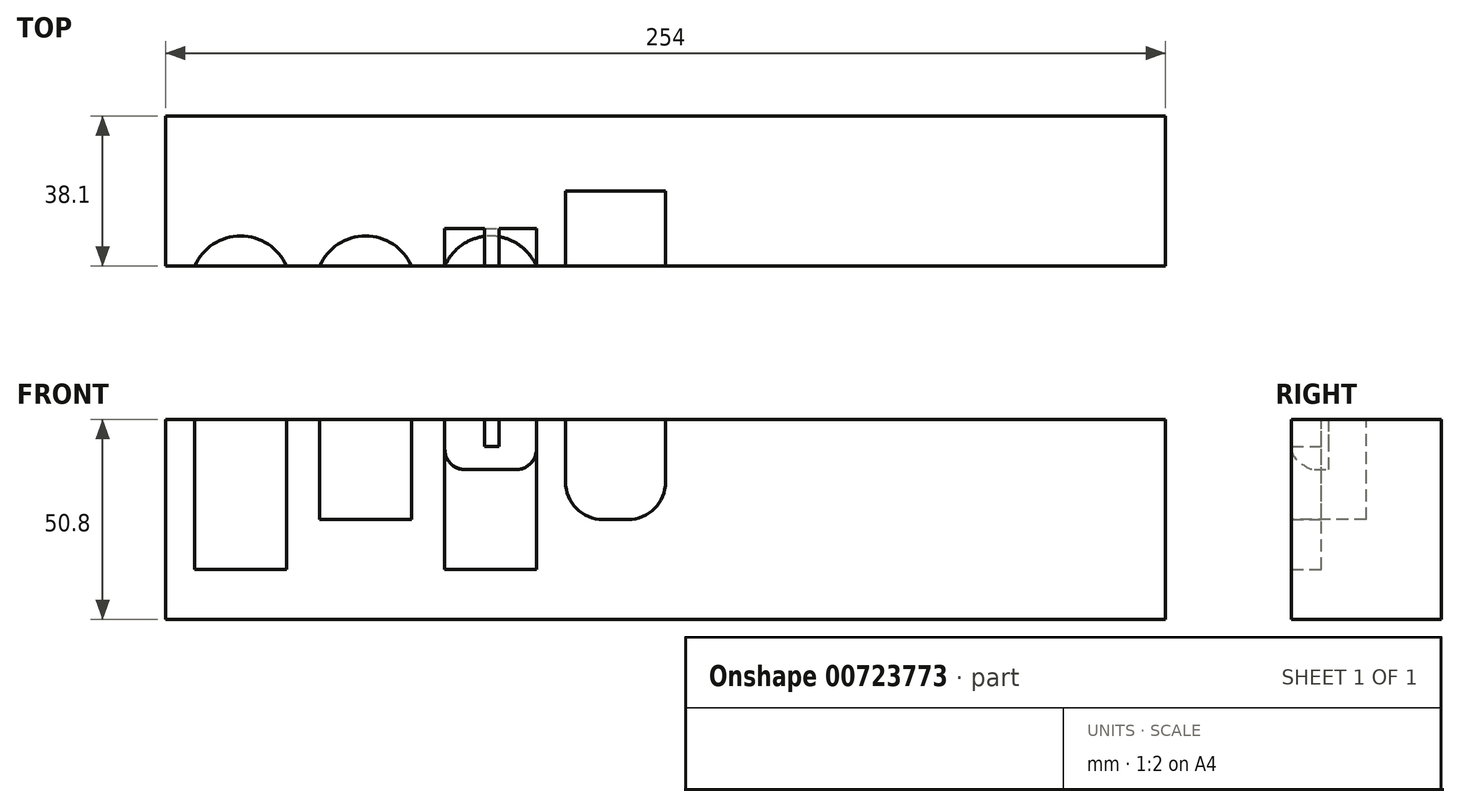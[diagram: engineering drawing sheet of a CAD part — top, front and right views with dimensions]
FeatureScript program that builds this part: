
annotation { "Feature Type Name" : "Feature", "Feature Type Description" : "" }
export const myFeature = defineFeature(function(context is Context, id is Id, definition is map)
    precondition{}
    {
        {
            var Q0;
            Q0=qCreatedBy(makeId("Right.planeOp"),FACE);
            var sketch = newSketch(context, id + "F0", { "sketchPlane" : qUnion([Q0])});
            skLineSegment(sketch, "E0.bottom", {"start": v(0, 0) * mm, "end": v(38.1, 0) * mm});
            skLineSegment(sketch, "E0.top", {"start": v(0, 50.8) * mm, "end": v(38.1, 50.8) * mm});
            skLineSegment(sketch, "E0.left", {"start": v(0, 0) * mm, "end": v(0, 50.8) * mm});
            skLineSegment(sketch, "E0.right", {"start": v(38.1, 0) * mm, "end": v(38.1, 50.8) * mm});
            skSolve(sketch);
        }
        {
            var Q0;
            Q0=makeQuery(id+"F0.imprint","IMPRINT",FACE,{"disambiguationData":[TD([[makeQuery(id+"F0.imprint","IMPRINT",EDGE,{"derivedFrom":sQuery(id+"F0.wireOp",EDGE,"E0.bottom")}),1.0]])]});
            extrude(context, id + "F1", {"entities" : qUnion([Q0]), "depth" : 254 * mm, "offsetDistance" : 25.4 * mm});
        }
        {
            var Q0;
            Q0=makeQuery(id+"F1.opExtrude","SWEPT_FACE",FACE,{"disambiguationData":[OSD([sQuery(id+"F0.wireOp",EDGE,"E0.top")])]});
            var sketch = newSketch(context, id + "F2", { "sketchPlane" : qUnion([Q0])});
            skLineSegment(sketch, "E1", {"start": v(0, 0) * mm, "end": v(0, -5.08) * mm});
            skLineSegment(sketch, "E2", {"start": v(0, -5.08) * mm, "end": v(19.05, -5.08) * mm});
            skCircle(sketch, "E3", {"center": v(19.05, -5.08) * mm, "radius": 12.7 * mm});
            skSolve(sketch);
        }
        {
            var Q0;
            Q0 = qSketchRegion(id + "F2", true);
            extrude(context, id + "F3", {"entities" : qUnion([Q0]), "operationType" : NewBodyOperationType.REMOVE, "oppositeDirection" : true, "depth" : 38.1 * mm, "offsetDistance" : 25.4 * mm});
        }
        {
            var Q0;
            Q0=makeQuery(id+"F1.opExtrude","SWEPT_FACE",FACE,{"disambiguationData":[OSD([sQuery(id+"F0.wireOp",EDGE,"E0.top")])]});
            var sketch = newSketch(context, id + "F4", { "sketchPlane" : qUnion([Q0])});
            skLineSegment(sketch, "E4", {"start": v(0, 0) * mm, "end": v(0, -5.08) * mm});
            skLineSegment(sketch, "E5", {"start": v(0, -5.08) * mm, "end": v(50.8, -5.08) * mm});
            skCircle(sketch, "E6", {"center": v(50.8, -5.08) * mm, "radius": 12.7 * mm});
            skSolve(sketch);
        }
        {
            var Q0;
            Q0 = qSketchRegion(id + "F4", true);
            extrude(context, id + "F5", {"entities" : qUnion([Q0]), "operationType" : NewBodyOperationType.REMOVE, "oppositeDirection" : true, "depth" : 25.4 * mm, "offsetDistance" : 25.4 * mm});
        }
        {
            var Q0;
            Q0=makeQuery(id+"F1.opExtrude","SWEPT_FACE",FACE,{"disambiguationData":[OSD([sQuery(id+"F0.wireOp",EDGE,"E0.top")])]});
            var sketch = newSketch(context, id + "F6", { "sketchPlane" : qUnion([Q0])});
            skLineSegment(sketch, "E7", {"start": v(0, 0) * mm, "end": v(0, -5.08) * mm});
            skLineSegment(sketch, "E8", {"start": v(0, -5.08) * mm, "end": v(82.55, -5.08) * mm});
            skCircle(sketch, "E9", {"center": v(82.55, -5.08) * mm, "radius": 12.7 * mm});
            skSolve(sketch);
        }
        {
            var Q0;
            Q0 = qSketchRegion(id + "F6", true);
            extrude(context, id + "F7", {"entities" : qUnion([Q0]), "operationType" : NewBodyOperationType.REMOVE, "oppositeDirection" : true, "depth" : 38.1 * mm, "offsetDistance" : 25.4 * mm});
        }
        {
            var Q0;
            Q0=makeQuery(id+"F1.opExtrude","SWEPT_FACE",FACE,{"disambiguationData":[OSD([sQuery(id+"F0.wireOp",EDGE,"E0.top")])]});
            var sketch = newSketch(context, id + "F8", { "sketchPlane" : qUnion([Q0])});
            skLineSegment(sketch, "E10", {"start": v(0, 0) * mm, "end": v(0, -9.07) * mm});
            skLineSegment(sketch, "E11", {"start": v(70.91, 0) * mm, "end": v(70.91, -18.35) * mm});
            skLineSegment(sketch, "E12", {"start": v(0, -9.07) * mm, "end": v(70.91, -9.07) * mm});
            skPoint(sketch, "E12.endSnap0", {"position": v(70.91, -9.18) * mm});
            skLineSegment(sketch, "E13.bottom", {"start": v(70.91, -9.07) * mm, "end": v(94.19, -9.07) * mm});
            skLineSegment(sketch, "E13.top", {"start": v(70.91, 0) * mm, "end": v(94.19, 0) * mm});
            skLineSegment(sketch, "E13.left", {"start": v(70.91, -9.07) * mm, "end": v(70.91, 0) * mm});
            skLineSegment(sketch, "E13.right", {"start": v(94.19, -9.07) * mm, "end": v(94.19, 0) * mm});
            skLineSegment(sketch, "E14.bottom", {"start": v(94.19, 0) * mm, "end": v(70.91, 0) * mm});
            skLineSegment(sketch, "E14.top", {"start": v(94.19, 9.57) * mm, "end": v(70.91, 9.57) * mm});
            skLineSegment(sketch, "E14.left", {"start": v(94.19, 0) * mm, "end": v(94.19, 9.57) * mm});
            skLineSegment(sketch, "E14.right", {"start": v(70.91, 0) * mm, "end": v(70.91, 9.57) * mm});
            skSolve(sketch);
        }
        {
            var Q0;
            Q0 = qSketchRegion(id + "F8", true);
            extrude(context, id + "F9", {"entities" : qUnion([Q0]), "operationType" : NewBodyOperationType.REMOVE, "oppositeDirection" : true, "depth" : 12.7 * mm, "offsetDistance" : 25.4 * mm});
        }
        {
            var Q0;
            Q0=makeQuery(id+"F9.boolean.opBoolean","COPY",EDGE,{"derivedFrom":makeQuery(id+"F9.opExtrude","CAP_EDGE",EDGE,{"disambiguationData":[OSD([sQuery(id+"F8.wireOp",EDGE,"E13.left"),sQuery(id+"F8.wireOp",EDGE,"E14.right")])],"isStart":false})});
            var Q1;
            Q1=makeQuery(id+"F9.boolean.opBoolean","COPY",EDGE,{"derivedFrom":makeQuery(id+"F9.opExtrude","CAP_EDGE",EDGE,{"disambiguationData":[OSD([sQuery(id+"F8.wireOp",EDGE,"E13.right"),sQuery(id+"F8.wireOp",EDGE,"E14.left")])],"isStart":false})});
            fillet(context, id + "F10", {"entities" : qUnion([Q0, Q1]), "radius" : 5.08 * mm, "tangentPropagation" : true, "allowEdgeOverflow" : false});
        }
        {
            var Q0;
            Q0=makeQuery(id+"F9.boolean.opBoolean","COPY",FACE,{"derivedFrom":makeQuery(id+"F9.opExtrude","SWEPT_FACE",FACE,{"disambiguationData":[OSD([sQuery(id+"F8.wireOp",EDGE,"E14.top")])]})});
            var sketch = newSketch(context, id + "F11", { "sketchPlane" : qUnion([Q0])});
            skLineSegment(sketch, "E15", {"start": v(70.91, 50.8) * mm, "end": v(81.06, 50.8) * mm});
            skLineSegment(sketch, "E16", {"start": v(81.06, 50.8) * mm, "end": v(81.06, 43.95) * mm});
            skLineSegment(sketch, "E17", {"start": v(81.06, 43.95) * mm, "end": v(84.68, 43.95) * mm});
            skLineSegment(sketch, "E18", {"start": v(84.68, 43.95) * mm, "end": v(84.68, 50.8) * mm});
            skLineSegment(sketch, "E19", {"start": v(84.68, 50.8) * mm, "end": v(81.06, 50.8) * mm});
            skSolve(sketch);
        }
        {
            var Q0;
            Q0 = qSketchRegion(id + "F11", true);
            extrude(context, id + "F12", {"entities" : qUnion([Q0]), "operationType" : NewBodyOperationType.ADD, "depth" : 9.52 * mm, "offsetDistance" : 25.4 * mm});
        }
        {
            var Q0;
            Q0=makeQuery(id+"F1.opExtrude","SWEPT_FACE",FACE,{"disambiguationData":[OSD([sQuery(id+"F0.wireOp",EDGE,"E0.left")])]});
            var sketch = newSketch(context, id + "F13", { "sketchPlane" : qUnion([Q0])});
            skLineSegment(sketch, "E20", {"start": v(0, 50.8) * mm, "end": v(0, 38.1) * mm});
            skLineSegment(sketch, "E21", {"start": v(0, 38.1) * mm, "end": v(101.6, 38.1) * mm});
            skLineSegment(sketch, "E22", {"start": v(101.6, 38.1) * mm, "end": v(101.6, 50.8) * mm});
            skLineSegment(sketch, "E23", {"start": v(101.6, 50.8) * mm, "end": v(127, 50.8) * mm});
            skLineSegment(sketch, "E24", {"start": v(127, 50.8) * mm, "end": v(127, 25.4) * mm});
            skLineSegment(sketch, "E25", {"start": v(127, 25.4) * mm, "end": v(101.6, 25.4) * mm});
            skLineSegment(sketch, "E26", {"start": v(101.6, 25.4) * mm, "end": v(101.6, 38.1) * mm});
            skSolve(sketch);
        }
        {
            var Q0;
            Q0 = qSketchRegion(id + "F13", true);
            extrude(context, id + "F14", {"entities" : qUnion([Q0]), "operationType" : NewBodyOperationType.REMOVE, "oppositeDirection" : true, "depth" : 19.05 * mm, "offsetDistance" : 25.4 * mm});
        }
        {
            var Q0;
            Q0=makeQuery(id+"F14.boolean.opBoolean","COPY",EDGE,{"derivedFrom":makeQuery(id+"F14.opExtrude","SWEPT_EDGE",EDGE,{"disambiguationData":[OSD([sQuery(id+"F13.wireOp",EDGE,"E25"),sQuery(id+"F13.wireOp",EDGE,"E26")])]})});
            var Q1;
            Q1=makeQuery(id+"F14.boolean.opBoolean","COPY",EDGE,{"derivedFrom":makeQuery(id+"F14.opExtrude","SWEPT_EDGE",EDGE,{"disambiguationData":[OSD([sQuery(id+"F13.wireOp",EDGE,"E24"),sQuery(id+"F13.wireOp",EDGE,"E25")])]})});
            fillet(context, id + "F15", {"entities" : qUnion([Q0, Q1]), "radius" : 9.52 * mm, "tangentPropagation" : true, "allowEdgeOverflow" : false});
        }
    });
